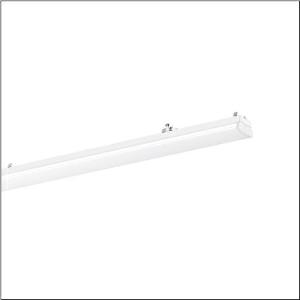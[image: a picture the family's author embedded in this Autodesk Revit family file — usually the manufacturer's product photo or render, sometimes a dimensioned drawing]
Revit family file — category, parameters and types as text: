
# Revit family: licross_r__21_recessed_opal_mo_52tl1d7n44xg_713e
name_source: partatom
category: Lighting Fixtures
units: mm (PartAtom-declared; Revit-internal decimal feet)

## family parameters
Cut with Voids When Loaded = No
Host = Face
Light Source = No
Part Type = Normal
Room Calculation Point = No
Round Connector Dimension = Use Diameter
Shared = No

## types (1)
- Licross® 21 recessed opal MO (1 x LED, 4400 lm, 24.7 W, 4000K)
    Apparent Load = 25 VA
    CIE Flux Codes = 44 73 91 87 100
    Color Rendering = 80
    Color Temperature = 4000K
    Default Elevation = 1800 mm
    Description = Licross® 21 recessed opal MO, luminaire insert, of sheet steel, galvanised, coil coated, white, length: 1.500mm, width: 66mm, height: 67mm, LED rated luminous flux: 4.400lm, light colour: 840, control gear: ON/OFF, with plug, 3-pole, with phase selection, mains connection: 220..240V, AC, 50/60Hz, rated input power: 25W, halogen-free wiring, primary optical cover: cover, of PMMA, light emission: direct with ceiling illumination distribution, primary light characteristic: symmetric, protection rating (complete): IP40, insulation class (complete): insulation class I (protective earthing), certification: CE, ENEC, VDE, UKCA, protection symbol: D if used in an environment without relevant dust loads with corresponding accessories, impact resistance: IK06, permissible ambient temperature for indoor applications: -35..+50°C, corresponds to IFS (International Featured Standards) requirements for safety and quality in the food industry, reducing of maximum allowable ambient temperature of 5°C with ceiling mounting, LABS conformity tested according to VDMA 24364:2018-05, packaging unit: 1 piece
    Height = 83 mm
    Lamp = 1 x LED
    Lamp Light Flux = 4400 lm
    Lamp Power = 24.7 W
    Lamp count = 1
    Length = 1500 mm
    Luminous efficacy = 178 lm/W
    Manufacturer = Siteco
    ModVariant = No
    Model = 52TL1D7N44XG
    Mounting Place = Ceiling
    Mounting Type = Pendant
    Number of Poles = 1
    OnlyDefault = Yes
    Power Factor = 1
    Product Name = Licross® 21 recessed opal MO
    Product group = luminaire insert
    ProductGroupID = 901
    Protection Class = Protection class I
    Protection Degree = IP 40
    RLX_Detail_Level = 1
    RLX_Emergency_Light_Flux = 0 lm
    RLX_Emergency_Type = 0
    RLX_Emergency_Type_DB = No
    RlxData = <blob elided: 23205 chars, md5=717acd05>
    Socket = socket
    Standby Power = 0 W
    System Light Flux = 4400 lm
    System Power = 25 W
    Type Comments = Product without accessories
    Type Image = l_1313666.jpg
    URL = http://relux.com
    VarID = ---
    Voltage = 0 V
    Weight = 0.00 kg
    Width = 76 mm

## geometry (parser evidence)
native form markers: Blend x4, Sweep x14
no freeform markers — native parametric forms only
